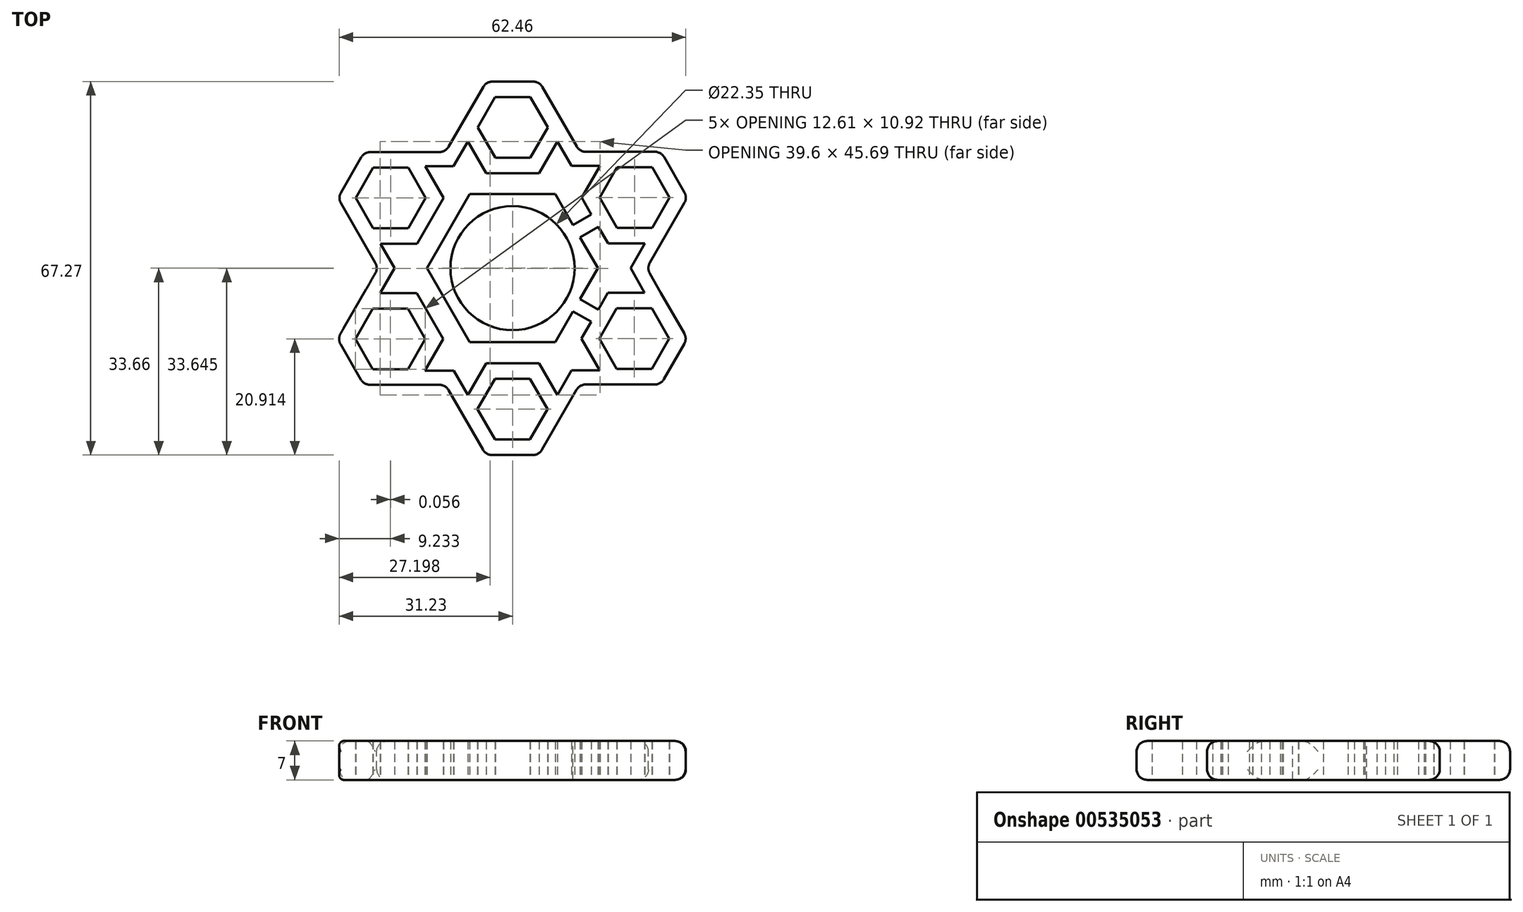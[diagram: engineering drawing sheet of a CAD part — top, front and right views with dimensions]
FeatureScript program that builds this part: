
annotation { "Feature Type Name" : "Feature", "Feature Type Description" : "" }
export const myFeature = defineFeature(function(context is Context, id is Id, definition is map)
    precondition{}
    {
        {
            var Q0;
            Q0=qCreatedBy(makeId("Top.planeOp"),FACE);
            var sketch = newSketch(context, id + "F0", { "sketchPlane" : qUnion([Q0])});
            skCircle(sketch, "E0", {"center": v(0, 0) * mm, "radius": 10.95 * mm});
            skCircle(sketch, "E1.cCircle", {"center": v(0, 0) * mm, "radius": 12.7 * mm, "construction": true});
            skLineSegment(sketch, "E1.0", {"start": v(-7.33, 12.7) * mm, "end": v(7.33, 12.7) * mm});
            skLineSegment(sketch, "E1.1", {"start": v(7.33, 12.7) * mm, "end": v(14.66, 0) * mm});
            skLineSegment(sketch, "E1.2", {"start": v(14.66, 0) * mm, "end": v(7.33, -12.7) * mm});
            skLineSegment(sketch, "E1.3", {"start": v(7.33, -12.7) * mm, "end": v(-7.33, -12.7) * mm});
            skLineSegment(sketch, "E1.4", {"start": v(-7.33, -12.7) * mm, "end": v(-14.66, 0) * mm});
            skLineSegment(sketch, "E1.5", {"start": v(-14.66, 0) * mm, "end": v(-7.33, 12.7) * mm});
            skPoint(sketch, "E1.0.midPoint", {"position": v(0, 12.7) * mm});
            skPoint(sketch, "E2.endSnap0", {"position": v(0, -12.7) * mm});
            skCircle(sketch, "E3.cCircle", {"center": v(0.06, 25.36) * mm, "radius": 5.46 * mm, "construction": true});
            skLineSegment(sketch, "E3.0", {"start": v(3.23, 19.9) * mm, "end": v(-3.08, 19.88) * mm});
            skLineSegment(sketch, "E3.1", {"start": v(-3.08, 19.88) * mm, "end": v(-6.25, 25.33) * mm});
            skLineSegment(sketch, "E3.2", {"start": v(-6.25, 25.33) * mm, "end": v(-3.12, 30.8) * mm});
            skLineSegment(sketch, "E3.3", {"start": v(-3.12, 30.8) * mm, "end": v(3.2, 30.83) * mm});
            skLineSegment(sketch, "E3.4", {"start": v(3.2, 30.83) * mm, "end": v(6.36, 25.38) * mm});
            skLineSegment(sketch, "E3.5", {"start": v(6.36, 25.38) * mm, "end": v(3.23, 19.9) * mm});
            skPoint(sketch, "E3.0.midPoint", {"position": v(0.07, 19.9) * mm});
            skCircle(sketch, "E4.cCircle", {"center": v(22, 12.7) * mm, "radius": 5.46 * mm, "construction": true});
            skLineSegment(sketch, "E4.0", {"start": v(18.84, 7.24) * mm, "end": v(15.7, 12.7) * mm});
            skLineSegment(sketch, "E4.1", {"start": v(15.7, 12.7) * mm, "end": v(18.84, 18.16) * mm});
            skLineSegment(sketch, "E4.2", {"start": v(18.84, 18.16) * mm, "end": v(25.15, 18.16) * mm});
            skLineSegment(sketch, "E4.3", {"start": v(25.15, 18.16) * mm, "end": v(28.3, 12.7) * mm});
            skLineSegment(sketch, "E4.4", {"start": v(28.3, 12.7) * mm, "end": v(25.15, 7.24) * mm});
            skLineSegment(sketch, "E4.5", {"start": v(25.15, 7.24) * mm, "end": v(18.84, 7.24) * mm});
            skPoint(sketch, "E4.0.midPoint", {"position": v(17.27, 9.97) * mm});
            skCircle(sketch, "E5.cCircle", {"center": v(21.94, -12.7) * mm, "radius": 5.46 * mm, "construction": true});
            skLineSegment(sketch, "E5.0", {"start": v(18.8, -18.16) * mm, "end": v(15.64, -12.7) * mm});
            skLineSegment(sketch, "E5.1", {"start": v(15.64, -12.7) * mm, "end": v(18.8, -7.24) * mm});
            skLineSegment(sketch, "E5.2", {"start": v(18.8, -7.24) * mm, "end": v(25.1, -7.24) * mm});
            skLineSegment(sketch, "E5.3", {"start": v(25.1, -7.24) * mm, "end": v(28.25, -12.7) * mm});
            skLineSegment(sketch, "E5.4", {"start": v(28.25, -12.7) * mm, "end": v(25.1, -18.16) * mm});
            skLineSegment(sketch, "E5.5", {"start": v(25.1, -18.16) * mm, "end": v(18.8, -18.16) * mm});
            skPoint(sketch, "E5.0.midPoint", {"position": v(17.22, -15.43) * mm});
            skCircle(sketch, "E6.cCircle", {"center": v(0, -25.4) * mm, "radius": 5.46 * mm, "construction": true});
            skLineSegment(sketch, "E6.0", {"start": v(-3.15, -19.94) * mm, "end": v(3.15, -19.94) * mm});
            skLineSegment(sketch, "E6.1", {"start": v(3.15, -19.94) * mm, "end": v(6.3, -25.4) * mm});
            skLineSegment(sketch, "E6.2", {"start": v(6.3, -25.4) * mm, "end": v(3.15, -30.86) * mm});
            skLineSegment(sketch, "E6.3", {"start": v(3.15, -30.86) * mm, "end": v(-3.15, -30.86) * mm});
            skLineSegment(sketch, "E6.4", {"start": v(-3.15, -30.86) * mm, "end": v(-6.3, -25.4) * mm});
            skLineSegment(sketch, "E6.5", {"start": v(-6.3, -25.4) * mm, "end": v(-3.15, -19.94) * mm});
            skPoint(sketch, "E6.0.midPoint", {"position": v(0, -19.94) * mm});
            skCircle(sketch, "E7.cCircle", {"center": v(-22, -12.75) * mm, "radius": 5.46 * mm, "construction": true});
            skLineSegment(sketch, "E7.0", {"start": v(-18.84, -7.28) * mm, "end": v(-15.7, -12.75) * mm});
            skLineSegment(sketch, "E7.1", {"start": v(-15.7, -12.75) * mm, "end": v(-18.84, -18.2) * mm});
            skLineSegment(sketch, "E7.2", {"start": v(-18.84, -18.2) * mm, "end": v(-25.15, -18.2) * mm});
            skLineSegment(sketch, "E7.3", {"start": v(-25.15, -18.2) * mm, "end": v(-28.3, -12.75) * mm});
            skLineSegment(sketch, "E7.4", {"start": v(-28.3, -12.75) * mm, "end": v(-25.15, -7.28) * mm});
            skLineSegment(sketch, "E7.5", {"start": v(-25.15, -7.28) * mm, "end": v(-18.84, -7.28) * mm});
            skPoint(sketch, "E7.0.midPoint", {"position": v(-17.27, -10.02) * mm});
            skCircle(sketch, "E8.cCircle", {"center": v(-21.94, 12.66) * mm, "radius": 5.46 * mm, "construction": true});
            skLineSegment(sketch, "E8.0", {"start": v(-15.64, 12.66) * mm, "end": v(-18.79, 7.2) * mm});
            skLineSegment(sketch, "E8.1", {"start": v(-18.79, 7.2) * mm, "end": v(-25.1, 7.2) * mm});
            skLineSegment(sketch, "E8.2", {"start": v(-25.1, 7.2) * mm, "end": v(-28.25, 12.66) * mm});
            skLineSegment(sketch, "E8.3", {"start": v(-28.25, 12.66) * mm, "end": v(-25.1, 18.12) * mm});
            skLineSegment(sketch, "E8.4", {"start": v(-25.1, 18.12) * mm, "end": v(-18.79, 18.12) * mm});
            skLineSegment(sketch, "E8.5", {"start": v(-18.79, 18.12) * mm, "end": v(-15.64, 12.66) * mm});
            skPoint(sketch, "E8.0.midPoint", {"position": v(-17.21, 9.93) * mm});
            skCircle(sketch, "E9.cCircle", {"center": v(-21.94, 12.66) * mm, "radius": 8.26 * mm, "construction": true});
            skLineSegment(sketch, "E9.0", {"start": v(-12.4, 12.66) * mm, "end": v(-17.18, 4.4) * mm});
            skLineSegment(sketch, "E9.1", {"start": v(-17.18, 4.4) * mm, "end": v(-26.7, 4.4) * mm});
            skLineSegment(sketch, "E9.2", {"start": v(-26.7, 4.4) * mm, "end": v(-31.47, 12.66) * mm});
            skLineSegment(sketch, "E9.3", {"start": v(-31.47, 12.66) * mm, "end": v(-26.7, 20.91) * mm});
            skLineSegment(sketch, "E9.4", {"start": v(-26.7, 20.91) * mm, "end": v(-17.18, 20.91) * mm});
            skLineSegment(sketch, "E9.5", {"start": v(-17.18, 20.91) * mm, "end": v(-12.4, 12.66) * mm});
            skPoint(sketch, "E9.0.midPoint", {"position": v(-14.8, 8.53) * mm});
            skCircle(sketch, "E10.cCircle", {"center": v(0.06, 25.36) * mm, "radius": 8.26 * mm, "construction": true});
            skLineSegment(sketch, "E10.0", {"start": v(4.82, 17.1) * mm, "end": v(-4.71, 17.1) * mm});
            skLineSegment(sketch, "E10.1", {"start": v(-4.71, 17.1) * mm, "end": v(-9.48, 25.36) * mm});
            skLineSegment(sketch, "E10.2", {"start": v(-9.48, 25.36) * mm, "end": v(-4.71, 33.61) * mm});
            skLineSegment(sketch, "E10.3", {"start": v(-4.71, 33.61) * mm, "end": v(4.82, 33.61) * mm});
            skLineSegment(sketch, "E10.4", {"start": v(4.82, 33.61) * mm, "end": v(9.59, 25.36) * mm});
            skLineSegment(sketch, "E10.5", {"start": v(9.59, 25.36) * mm, "end": v(4.82, 17.1) * mm});
            skPoint(sketch, "E10.0.midPoint", {"position": v(0.06, 17.1) * mm});
            skCircle(sketch, "E11.cCircle", {"center": v(22, 12.7) * mm, "radius": 8.26 * mm, "construction": true});
            skLineSegment(sketch, "E11.0", {"start": v(17.23, 4.45) * mm, "end": v(12.47, 12.7) * mm});
            skLineSegment(sketch, "E11.1", {"start": v(12.47, 12.7) * mm, "end": v(17.23, 20.96) * mm});
            skLineSegment(sketch, "E11.2", {"start": v(17.23, 20.96) * mm, "end": v(26.76, 20.96) * mm});
            skLineSegment(sketch, "E11.3", {"start": v(26.76, 20.96) * mm, "end": v(31.53, 12.7) * mm});
            skLineSegment(sketch, "E11.4", {"start": v(31.53, 12.7) * mm, "end": v(26.76, 4.45) * mm});
            skLineSegment(sketch, "E11.5", {"start": v(26.76, 4.45) * mm, "end": v(17.23, 4.45) * mm});
            skPoint(sketch, "E11.0.midPoint", {"position": v(14.85, 8.57) * mm});
            skCircle(sketch, "E12.cCircle", {"center": v(21.94, -12.7) * mm, "radius": 8.26 * mm, "construction": true});
            skLineSegment(sketch, "E12.0", {"start": v(12.41, -12.7) * mm, "end": v(17.18, -4.45) * mm});
            skLineSegment(sketch, "E12.1", {"start": v(17.18, -4.45) * mm, "end": v(26.71, -4.45) * mm});
            skLineSegment(sketch, "E12.2", {"start": v(26.71, -4.45) * mm, "end": v(31.48, -12.7) * mm});
            skLineSegment(sketch, "E12.3", {"start": v(31.48, -12.7) * mm, "end": v(26.71, -20.96) * mm});
            skLineSegment(sketch, "E12.4", {"start": v(26.71, -20.96) * mm, "end": v(17.18, -20.96) * mm});
            skLineSegment(sketch, "E12.5", {"start": v(17.18, -20.95) * mm, "end": v(12.41, -12.7) * mm});
            skPoint(sketch, "E12.0.midPoint", {"position": v(14.8, -8.57) * mm});
            skCircle(sketch, "E13.cCircle", {"center": v(0, -25.4) * mm, "radius": 8.26 * mm, "construction": true});
            skLineSegment(sketch, "E13.0", {"start": v(-4.77, -17.14) * mm, "end": v(4.77, -17.15) * mm});
            skLineSegment(sketch, "E13.1", {"start": v(4.77, -17.15) * mm, "end": v(9.53, -25.4) * mm});
            skLineSegment(sketch, "E13.2", {"start": v(9.53, -25.4) * mm, "end": v(4.77, -33.66) * mm});
            skLineSegment(sketch, "E13.3", {"start": v(4.77, -33.66) * mm, "end": v(-4.77, -33.65) * mm});
            skLineSegment(sketch, "E13.4", {"start": v(-4.77, -33.65) * mm, "end": v(-9.53, -25.4) * mm});
            skLineSegment(sketch, "E13.5", {"start": v(-9.53, -25.4) * mm, "end": v(-4.77, -17.14) * mm});
            skPoint(sketch, "E13.0.midPoint", {"position": v(0, -17.15) * mm});
            skCircle(sketch, "E14.cCircle", {"center": v(-22, -12.75) * mm, "radius": 8.26 * mm, "construction": true});
            skLineSegment(sketch, "E14.0", {"start": v(-17.23, -4.5) * mm, "end": v(-12.46, -12.75) * mm});
            skLineSegment(sketch, "E14.1", {"start": v(-12.46, -12.75) * mm, "end": v(-17.23, -21) * mm});
            skLineSegment(sketch, "E14.2", {"start": v(-17.23, -21) * mm, "end": v(-26.76, -21) * mm});
            skLineSegment(sketch, "E14.3", {"start": v(-26.76, -21) * mm, "end": v(-31.53, -12.75) * mm});
            skLineSegment(sketch, "E14.4", {"start": v(-31.53, -12.75) * mm, "end": v(-26.76, -4.5) * mm});
            skLineSegment(sketch, "E14.5", {"start": v(-26.76, -4.5) * mm, "end": v(-17.23, -4.5) * mm});
            skPoint(sketch, "E14.0.midPoint", {"position": v(-14.85, -8.62) * mm});
            skLineSegment(sketch, "E15", {"start": v(-14.25, 15.84) * mm, "end": v(-15.43, 17.88) * mm});
            skLineSegment(sketch, "E16", {"start": v(-23.27, -4.5) * mm, "end": v(-20.73, -4.5) * mm});
            skLineSegment(sketch, "E17", {"start": v(-7.78, -22.37) * mm, "end": v(-6.51, -20.17) * mm});
            skLineSegment(sketch, "E18", {"start": v(14.16, -15.73) * mm, "end": v(15.43, -17.93) * mm});
            skLineSegment(sketch, "E19", {"start": v(20.73, 4.45) * mm, "end": v(23.27, 4.45) * mm});
            skLineSegment(sketch, "E20", {"start": v(6.61, 20.2) * mm, "end": v(7.88, 22.4) * mm});
            skLineSegment(sketch, "E21.bottom", {"start": v(-1.27, -12.7) * mm, "end": v(1.27, -12.7) * mm});
            skLineSegment(sketch, "E21.top", {"start": v(-1.27, -17.15) * mm, "end": v(1.27, -17.15) * mm});
            skLineSegment(sketch, "E22.bottom", {"start": v(1.27, 12.7) * mm, "end": v(-1.27, 12.7) * mm});
            skLineSegment(sketch, "E22.top", {"start": v(1.24, 17.1) * mm, "end": v(-1.3, 17.1) * mm});
            skLineSegment(sketch, "E23", {"start": v(14.21, 9.67) * mm, "end": v(10.3, 7.42) * mm});
            skLineSegment(sketch, "E24", {"start": v(10.3, 7.42) * mm, "end": v(11.63, 5.25) * mm});
            skLineSegment(sketch, "E25", {"start": v(11.63, 5.25) * mm, "end": v(15.48, 7.47) * mm});
            skLineSegment(sketch, "E26", {"start": v(15.44, -7.45) * mm, "end": v(11.58, -5.22) * mm});
            skLineSegment(sketch, "E27", {"start": v(11.58, -5.22) * mm, "end": v(10.36, -7.45) * mm});
            skLineSegment(sketch, "E28", {"start": v(10.36, -7.45) * mm, "end": v(14.17, -9.65) * mm});
            skLineSegment(sketch, "E29", {"start": v(-10.36, -7.45) * mm, "end": v(-14.23, -9.68) * mm});
            skLineSegment(sketch, "E30", {"start": v(-14.23, -9.68) * mm, "end": v(-15.5, -7.48) * mm});
            skLineSegment(sketch, "E31", {"start": v(-15.5, -7.48) * mm, "end": v(-11.63, -5.25) * mm});
            skLineSegment(sketch, "E32", {"start": v(-11.6, 5.32) * mm, "end": v(-15.38, 7.5) * mm});
            skLineSegment(sketch, "E33", {"start": v(-15.38, 7.5) * mm, "end": v(-14.11, 9.7) * mm});
            skLineSegment(sketch, "E34", {"start": v(-14.11, 9.7) * mm, "end": v(-10.32, 7.52) * mm});
            skLineSegment(sketch, "E35", {"start": v(-11.6, 5.32) * mm, "end": v(-10.32, 7.52) * mm});
            skLineSegment(sketch, "E36", {"start": v(-14.11, 9.7) * mm, "end": v(-15.38, 7.5) * mm});
            skLineSegment(sketch, "E37", {"start": v(15.48, 7.47) * mm, "end": v(14.21, 9.67) * mm});
            skLineSegment(sketch, "E38", {"start": v(-11.63, -5.25) * mm, "end": v(-15.5, -7.48) * mm});
            skLineSegment(sketch, "E39", {"start": v(-15.5, -7.48) * mm, "end": v(-14.23, -9.68) * mm});
            skLineSegment(sketch, "E40", {"start": v(-14.23, -9.68) * mm, "end": v(-10.36, -7.45) * mm});
            skLineSegment(sketch, "E41", {"start": v(-10.36, -7.45) * mm, "end": v(-11.63, -5.25) * mm});
            skCircle(sketch, "E42", {"center": v(0, 0) * mm, "radius": 11.08 * mm});
            skCircle(sketch, "E43", {"center": v(0, 0) * mm, "radius": 11.07 * mm});
            skLineSegment(sketch, "E44", {"start": v(-17.18, 20.91) * mm, "end": v(-12.1, 20.91) * mm});
            skLineSegment(sketch, "E45", {"start": v(-12.1, 20.91) * mm, "end": v(-9.48, 25.36) * mm});
            skLineSegment(sketch, "E46", {"start": v(-8.02, 22.83) * mm, "end": v(-10.64, 18.37) * mm});
            skLineSegment(sketch, "E47", {"start": v(-10.64, 18.37) * mm, "end": v(-15.7, 18.37) * mm});
            skLineSegment(sketch, "E48", {"start": v(9.59, 25.36) * mm, "end": v(12.13, 20.96) * mm});
            skLineSegment(sketch, "E49", {"start": v(17.23, 20.96) * mm, "end": v(12.13, 20.96) * mm});
            skLineSegment(sketch, "E50", {"start": v(15.77, 18.42) * mm, "end": v(10.66, 18.42) * mm});
            skLineSegment(sketch, "E51", {"start": v(10.66, 18.42) * mm, "end": v(8.12, 22.82) * mm});
            skLineSegment(sketch, "E52", {"start": v(26.76, 4.45) * mm, "end": v(24.2, 0) * mm});
            skLineSegment(sketch, "E53", {"start": v(24.2, 0) * mm, "end": v(26.71, -4.45) * mm});
            skLineSegment(sketch, "E54", {"start": v(23.85, 4.45) * mm, "end": v(21.28, 0) * mm});
            skLineSegment(sketch, "E55", {"start": v(21.28, 0) * mm, "end": v(23.8, -4.45) * mm});
            skLineSegment(sketch, "E56", {"start": v(17.18, -20.96) * mm, "end": v(12.1, -20.96) * mm});
            skLineSegment(sketch, "E57", {"start": v(12.1, -20.96) * mm, "end": v(9.53, -25.4) * mm});
            skLineSegment(sketch, "E58", {"start": v(8.07, -22.86) * mm, "end": v(10.63, -18.42) * mm});
            skLineSegment(sketch, "E59", {"start": v(10.63, -18.42) * mm, "end": v(15.71, -18.42) * mm});
            skLineSegment(sketch, "E60", {"start": v(-17.23, -21) * mm, "end": v(-12.07, -21) * mm});
            skLineSegment(sketch, "E61", {"start": v(-12.07, -21) * mm, "end": v(-9.53, -25.4) * mm});
            skLineSegment(sketch, "E62", {"start": v(-8.07, -22.86) * mm, "end": v(-10.6, -18.46) * mm});
            skLineSegment(sketch, "E63", {"start": v(-10.6, -18.46) * mm, "end": v(-15.76, -18.46) * mm});
            skLineSegment(sketch, "E64", {"start": v(-26.76, -4.5) * mm, "end": v(-24.17, 0) * mm});
            skLineSegment(sketch, "E65", {"start": v(-24.17, 0) * mm, "end": v(-26.7, 4.4) * mm});
            skLineSegment(sketch, "E66", {"start": v(-23.77, 4.4) * mm, "end": v(-21.24, 0) * mm});
            skLineSegment(sketch, "E67", {"start": v(-21.24, 0) * mm, "end": v(-23.83, -4.5) * mm});
            skSolve(sketch);
        }
        {
            var Q0;
            Q0=qSketchRegion(id+"F0",true);
            var Q1;
            Q1=makeQuery(id+"F0.imprint","IMPRINT",FACE,{"disambiguationData":[TD([[makeQuery(id+"F0.imprint","IMPRINT",EDGE,{"derivedFrom":sQuery(id+"F0.wireOp",EDGE,"E22.bottom")}),-1.0]])]});
            var Q2;
            Q2=makeQuery(id+"F0.imprint","IMPRINT",FACE,{"disambiguationData":[TD([[makeQuery(id+"F0.imprint","IMPRINT",EDGE,{"derivedFrom":sQuery(id+"F0.wireOp",EDGE,"E38")}),1.0]])]});
            var Q3;
            Q3=makeQuery(id+"F0.imprint","IMPRINT",FACE,{"disambiguationData":[TD([[makeQuery(id+"F0.imprint","IMPRINT",EDGE,{"derivedFrom":sQuery(id+"F0.wireOp",EDGE,"E21.bottom")}),-1.0]])]});
            var Q4;
            {var subQ0=sQuery(id+"F0.wireOp",EDGE,"E28");Q4=makeQuery(id+"F0.imprint","IMPRINT",FACE,{"disambiguationData":[TD([[makeQuery(id+"F0.imprint","IMPRINT",EDGE,{"derivedFrom":subQ0}),1.0]])]});}
            var Q5;
            {var subQ0=sQuery(id+"F0.wireOp",EDGE,"E25");Q5=makeQuery(id+"F0.imprint","IMPRINT",FACE,{"disambiguationData":[TD([[makeQuery(id+"F0.imprint","IMPRINT",EDGE,{"derivedFrom":subQ0}),1.0]])]});}
            var Q6;
            Q6=makeQuery(id+"F0.imprint","IMPRINT",FACE,{"disambiguationData":[TD([[makeQuery(id+"F0.imprint","IMPRINT",EDGE,{"derivedFrom":sQuery(id+"F0.wireOp",EDGE,"E34")}),-1.0]])]});
            extrude(context, id + "F1", {"entities" : qUnion([Q0, Q1, Q2, Q3, Q4, Q5, Q6]), "depth" : 7 * mm, "offsetDistance" : 25.4 * mm});
        }
        {
            var Q0;
            Q0=qCreatedBy(makeId("Top.planeOp"),FACE);
            var sketch = newSketch(context, id + "F2", { "sketchPlane" : qUnion([Q0])});
            skCircle(sketch, "E68", {"center": v(0, 0) * mm, "radius": 11.18 * mm});
            skCircle(sketch, "E69.cCircle", {"center": v(0, 0) * mm, "radius": 13.34 * mm, "construction": true});
            skLineSegment(sketch, "E69.0", {"start": v(-7.7, 13.33) * mm, "end": v(7.7, 13.34) * mm});
            skLineSegment(sketch, "E69.1", {"start": v(7.7, 13.34) * mm, "end": v(15.4, 0) * mm});
            skLineSegment(sketch, "E69.2", {"start": v(15.4, 0) * mm, "end": v(7.7, -13.33) * mm});
            skLineSegment(sketch, "E69.3", {"start": v(7.7, -13.33) * mm, "end": v(-7.7, -13.34) * mm});
            skLineSegment(sketch, "E69.4", {"start": v(-7.7, -13.34) * mm, "end": v(-15.4, 0) * mm});
            skLineSegment(sketch, "E69.5", {"start": v(-15.4, 0) * mm, "end": v(-7.7, 13.33) * mm});
            skPoint(sketch, "E69.0.midPoint", {"position": v(0, 13.33) * mm});
            skSolve(sketch);
        }
        {
            var Q0;
            Q0=qSketchRegion(id+"F2",true);
            extrude(context, id + "F3", {"entities" : qUnion([Q0]), "operationType" : NewBodyOperationType.ADD, "depth" : 7 * mm});
        }
        {
            var Q0;
            Q0=makeQuery(id+"F1.opExtrude","CAP_EDGE",EDGE,{"disambiguationData":[OSD([sQuery(id+"F0.wireOp",EDGE,"E9.2")])],"isStart":false});
            var Q1;
            Q1=makeQuery(id+"F1.opExtrude","CAP_EDGE",EDGE,{"disambiguationData":[OSD([sQuery(id+"F0.wireOp",EDGE,"E65")])],"isStart":false});
            var Q2;
            Q2=makeQuery(id+"F1.opExtrude","CAP_EDGE",EDGE,{"disambiguationData":[OSD([sQuery(id+"F0.wireOp",EDGE,"E65")])],"isStart":true});
            var Q3;
            Q3=makeQuery(id+"F1.opExtrude","CAP_EDGE",EDGE,{"disambiguationData":[OSD([sQuery(id+"F0.wireOp",EDGE,"E9.2")])],"isStart":true});
            var Q4;
            Q4=makeQuery(id+"F1.opExtrude","SWEPT_EDGE",EDGE,{"disambiguationData":[OSD([sQuery(id+"F0.wireOp",EDGE,"E64"),sQuery(id+"F0.wireOp",EDGE,"E65")])]});
            var Q5;
            Q5=makeQuery(id+"F1.opExtrude","SWEPT_EDGE",EDGE,{"disambiguationData":[OSD([sQuery(id+"F0.wireOp",EDGE,"E60"),sQuery(id+"F0.wireOp",EDGE,"E61")])]});
            var Q6;
            Q6=makeQuery(id+"F1.opExtrude","SWEPT_FACE",FACE,{"disambiguationData":[OSD([sQuery(id+"F0.wireOp",EDGE,"E14.3")])]});
            var Q7;
            Q7=makeQuery(id+"F1.opExtrude","SWEPT_FACE",FACE,{"disambiguationData":[OSD([sQuery(id+"F0.wireOp",EDGE,"E14.2"),sQuery(id+"F0.wireOp",EDGE,"E60")])]});
            var Q8;
            Q8=makeQuery(id+"F1.opExtrude","SWEPT_FACE",FACE,{"disambiguationData":[OSD([sQuery(id+"F0.wireOp",EDGE,"E13.4"),sQuery(id+"F0.wireOp",EDGE,"E61")])]});
            var Q9;
            Q9=makeQuery(id+"F1.opExtrude","SWEPT_FACE",FACE,{"disambiguationData":[OSD([sQuery(id+"F0.wireOp",EDGE,"E13.3")])]});
            var Q10;
            Q10=makeQuery(id+"F1.opExtrude","SWEPT_FACE",FACE,{"disambiguationData":[OSD([sQuery(id+"F0.wireOp",EDGE,"E13.2"),sQuery(id+"F0.wireOp",EDGE,"E57")])]});
            var Q11;
            Q11=makeQuery(id+"F1.opExtrude","SWEPT_FACE",FACE,{"disambiguationData":[OSD([sQuery(id+"F0.wireOp",EDGE,"E12.4"),sQuery(id+"F0.wireOp",EDGE,"E56")])]});
            var Q12;
            Q12=makeQuery(id+"F1.opExtrude","SWEPT_EDGE",EDGE,{"disambiguationData":[OSD([sQuery(id+"F0.wireOp",EDGE,"E56"),sQuery(id+"F0.wireOp",EDGE,"E57")])]});
            var Q13;
            Q13=makeQuery(id+"F1.opExtrude","SWEPT_FACE",FACE,{"disambiguationData":[OSD([sQuery(id+"F0.wireOp",EDGE,"E12.3")])]});
            var Q14;
            Q14=makeQuery(id+"F1.opExtrude","SWEPT_FACE",FACE,{"disambiguationData":[OSD([sQuery(id+"F0.wireOp",EDGE,"E12.2")])]});
            var Q15;
            Q15=makeQuery(id+"F1.opExtrude","SWEPT_FACE",FACE,{"disambiguationData":[OSD([sQuery(id+"F0.wireOp",EDGE,"E53")])]});
            var Q16;
            Q16=makeQuery(id+"F1.opExtrude","SWEPT_EDGE",EDGE,{"disambiguationData":[OSD([sQuery(id+"F0.wireOp",EDGE,"E52"),sQuery(id+"F0.wireOp",EDGE,"E53")])]});
            var Q17;
            Q17=makeQuery(id+"F1.opExtrude","SWEPT_FACE",FACE,{"disambiguationData":[OSD([sQuery(id+"F0.wireOp",EDGE,"E11.4"),sQuery(id+"F0.wireOp",EDGE,"E52")])]});
            var Q18;
            Q18=makeQuery(id+"F1.opExtrude","SWEPT_FACE",FACE,{"disambiguationData":[OSD([sQuery(id+"F0.wireOp",EDGE,"E11.3")])]});
            var Q19;
            Q19=makeQuery(id+"F1.opExtrude","SWEPT_FACE",FACE,{"disambiguationData":[OSD([sQuery(id+"F0.wireOp",EDGE,"E11.2"),sQuery(id+"F0.wireOp",EDGE,"E49")])]});
            var Q20;
            Q20=makeQuery(id+"F1.opExtrude","SWEPT_EDGE",EDGE,{"disambiguationData":[OSD([sQuery(id+"F0.wireOp",EDGE,"E48"),sQuery(id+"F0.wireOp",EDGE,"E49")])]});
            var Q21;
            Q21=makeQuery(id+"F1.opExtrude","SWEPT_FACE",FACE,{"disambiguationData":[OSD([sQuery(id+"F0.wireOp",EDGE,"E10.4"),sQuery(id+"F0.wireOp",EDGE,"E48")])]});
            var Q22;
            Q22=makeQuery(id+"F1.opExtrude","SWEPT_FACE",FACE,{"disambiguationData":[OSD([sQuery(id+"F0.wireOp",EDGE,"E10.3")])]});
            var Q23;
            Q23=makeQuery(id+"F1.opExtrude","SWEPT_FACE",FACE,{"disambiguationData":[OSD([sQuery(id+"F0.wireOp",EDGE,"E10.2")])]});
            var Q24;
            Q24=makeQuery(id+"F1.opExtrude","SWEPT_FACE",FACE,{"disambiguationData":[OSD([sQuery(id+"F0.wireOp",EDGE,"E45")])]});
            var Q25;
            Q25=makeQuery(id+"F1.opExtrude","SWEPT_EDGE",EDGE,{"disambiguationData":[OSD([sQuery(id+"F0.wireOp",EDGE,"E44"),sQuery(id+"F0.wireOp",EDGE,"E45")])]});
            var Q26;
            Q26=makeQuery(id+"F1.opExtrude","SWEPT_FACE",FACE,{"disambiguationData":[OSD([sQuery(id+"F0.wireOp",EDGE,"E9.4"),sQuery(id+"F0.wireOp",EDGE,"E44")])]});
            var Q27;
            Q27=makeQuery(id+"F1.opExtrude","SWEPT_FACE",FACE,{"disambiguationData":[OSD([sQuery(id+"F0.wireOp",EDGE,"E9.3")])]});
            fillet(context, id + "F4", {"entities" : qUnion([Q0, Q1, Q2, Q3, Q4, Q5, Q6, Q7, Q8, Q9, Q10, Q11, Q12, Q13, Q14, Q15, Q16, Q17, Q18, Q19, Q20, Q21, Q22, Q23, Q24, Q25, Q26, Q27]), "radius" : 1.9 * mm, "tangentPropagation" : true, "allowEdgeOverflow" : false});
        }
    });
